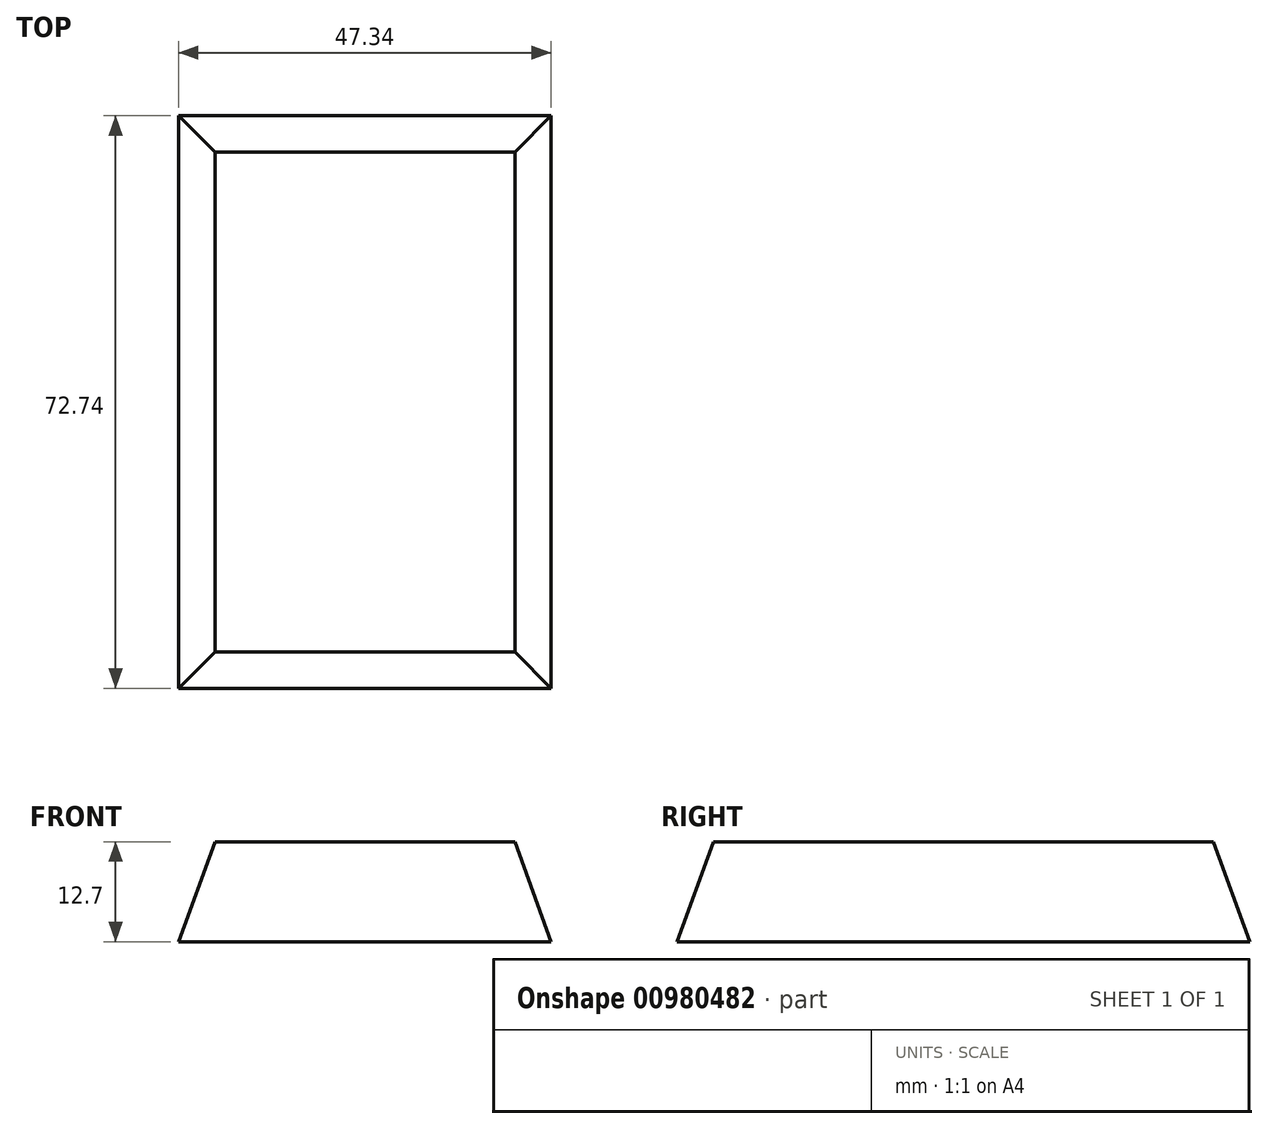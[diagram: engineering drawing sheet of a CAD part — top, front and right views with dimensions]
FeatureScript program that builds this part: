
annotation { "Feature Type Name" : "Feature", "Feature Type Description" : "" }
export const myFeature = defineFeature(function(context is Context, id is Id, definition is map)
    precondition{}
    {
        {
            var Q0;
            Q0=qCreatedBy(makeId("Top.planeOp"),FACE);
            var sketch = newSketch(context, id + "F0", { "sketchPlane" : qUnion([Q0])});
            skLineSegment(sketch, "E0.bottom", {"start": v(0, 0) * mm, "end": v(50.8, 0) * mm});
            skLineSegment(sketch, "E0.top", {"start": v(0, 76.2) * mm, "end": v(50.8, 76.2) * mm});
            skLineSegment(sketch, "E0.left", {"start": v(0, 0) * mm, "end": v(0, 76.2) * mm});
            skLineSegment(sketch, "E0.right", {"start": v(50.8, 0) * mm, "end": v(50.8, 76.2) * mm});
            skSolve(sketch);
        }
        {
            var Q0;
            Q0=makeQuery(id+"F0.imprint","IMPRINT",FACE,{"disambiguationData":[TD([[makeQuery(id+"F0.imprint","IMPRINT",EDGE,{"derivedFrom":sQuery(id+"F0.wireOp",EDGE,"E0.bottom")}),1.0]])]});
            extrude(context, id + "F1", {"entities" : qUnion([Q0]), "depth" : 12.7 * mm, "offsetDistance" : 25.4 * mm});
        }
        {
            var Q0;
            Q0=makeQuery(id+"F1.opExtrude","CAP_FACE",FACE,{"disambiguationData":[OSD([sQuery(id+"F0.wireOp",EDGE,"E0.bottom"),sQuery(id+"F0.wireOp",EDGE,"E0.top"),sQuery(id+"F0.wireOp",EDGE,"E0.left"),sQuery(id+"F0.wireOp",EDGE,"E0.right")])],"isStart":false});
            chamfer(context, id + "F2", {"entities" : qUnion([Q0]), "chamferType" : ChamferType.OFFSET_ANGLE, "width" : 6.35 * mm, "oppositeDirection" : false, "angle" : 70 * degree, "tangentPropagation" : true});
        }
    });
